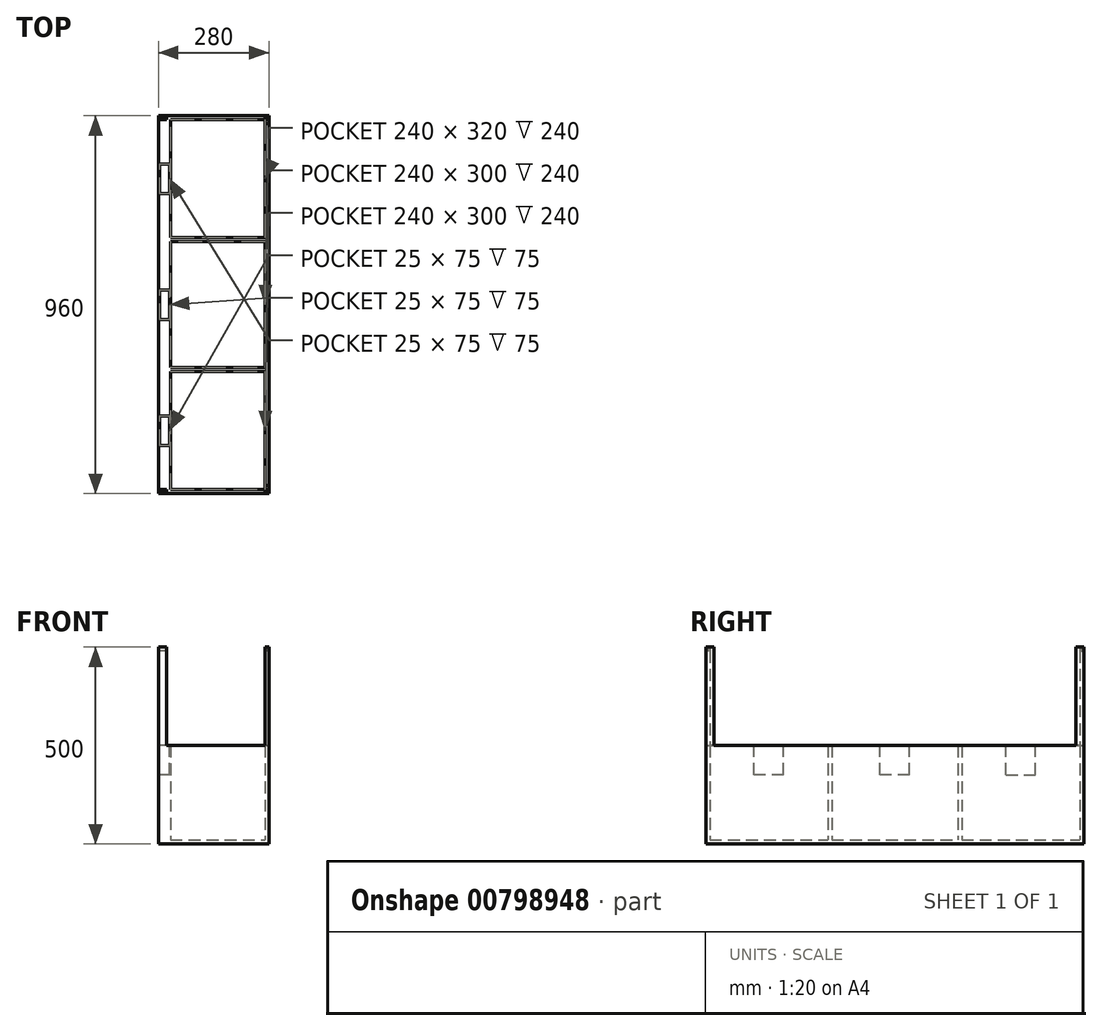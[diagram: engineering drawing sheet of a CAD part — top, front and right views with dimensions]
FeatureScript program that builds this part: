
annotation { "Feature Type Name" : "Feature", "Feature Type Description" : "" }
export const myFeature = defineFeature(function(context is Context, id is Id, definition is map)
    precondition{}
    {
        {
            var Q0;
            Q0=qCreatedBy(makeId("Top.planeOp"),FACE);
            var sketch = newSketch(context, id + "F0", { "sketchPlane" : qUnion([Q0])});
            skLineSegment(sketch, "E0.bottom", {"start": v(130, -480) * mm, "end": v(-130, -480) * mm});
            skLineSegment(sketch, "E0.top", {"start": v(130, 480) * mm, "end": v(-130, 480) * mm});
            skLineSegment(sketch, "E0.left", {"start": v(130, -480) * mm, "end": v(130, 480) * mm});
            skLineSegment(sketch, "E0.right", {"start": v(-130, -480) * mm, "end": v(-130, 480) * mm});
            skPoint(sketch, "E0.middle", {"position": v(0, 0) * mm});
            skLineSegment(sketch, "E1.bottom", {"start": v(-130, 480) * mm, "end": v(-150, 480) * mm});
            skLineSegment(sketch, "E1.top", {"start": v(-130, -480) * mm, "end": v(-150, -480) * mm});
            skLineSegment(sketch, "E1.left", {"start": v(-130, 480) * mm, "end": v(-130, -480) * mm});
            skLineSegment(sketch, "E1.right", {"start": v(-150, 480) * mm, "end": v(-150, -480) * mm});
            skSolve(sketch);
        }
        {
            var Q0;
            Q0=makeQuery(id+"F0.imprint","IMPRINT",FACE,{"disambiguationData":[TD([[makeQuery(id+"F0.imprint","IMPRINT",EDGE,{"derivedFrom":sQuery(id+"F0.wireOp",EDGE,"E0.bottom")}),-1.0]])]});
            extrude(context, id + "F1", {"entities" : qUnion([Q0]), "depth" : 250 * mm, "offsetDistance" : 25 * mm});
        }
        {
            var Q0;
            Q0=makeQuery(id+"F1.opExtrude","CAP_FACE",FACE,{"disambiguationData":[OSD([sQuery(id+"F0.wireOp",EDGE,"E0.bottom"),sQuery(id+"F0.wireOp",EDGE,"E0.top"),sQuery(id+"F0.wireOp",EDGE,"E0.left"),sQuery(id+"F0.wireOp",EDGE,"E0.right")])],"isStart":false});
            shell(context, id + "F2", {"entities" : qUnion([Q0]), "thickness" : 10 * mm});
        }
        {
            var Q0;
            Q0=makeQuery(id+"F2.opShell","OFFSET_FACE",FACE,{"disambiguationData":[OSD([sQuery(id+"F0.wireOp",EDGE,"E0.bottom"),sQuery(id+"F0.wireOp",EDGE,"E0.top"),sQuery(id+"F0.wireOp",EDGE,"E0.left"),sQuery(id+"F0.wireOp",EDGE,"E0.right")])]});
            var sketch = newSketch(context, id + "F3", { "sketchPlane" : qUnion([Q0])});
            skLineSegment(sketch, "E2.bottom", {"start": v(-120, 170) * mm, "end": v(120, 170) * mm});
            skLineSegment(sketch, "E2.top", {"start": v(-120, 160) * mm, "end": v(120, 160) * mm});
            skLineSegment(sketch, "E2.left", {"start": v(-120, 170) * mm, "end": v(-120, 160) * mm});
            skLineSegment(sketch, "E2.right", {"start": v(120, 170) * mm, "end": v(120, 160) * mm});
            skLineSegment(sketch, "E3.bottom", {"start": v(-120, -160) * mm, "end": v(120, -160) * mm});
            skLineSegment(sketch, "E3.top", {"start": v(-120, -170) * mm, "end": v(120, -170) * mm});
            skLineSegment(sketch, "E3.left", {"start": v(-120, -160) * mm, "end": v(-120, -170) * mm});
            skLineSegment(sketch, "E3.right", {"start": v(120, -160) * mm, "end": v(120, -170) * mm});
            skSolve(sketch);
        }
        {
            var Q0;
            Q0=makeQuery(id+"F3.imprint","IMPRINT",FACE,{"disambiguationData":[TD([[makeQuery(id+"F3.imprint","IMPRINT",EDGE,{"derivedFrom":sQuery(id+"F3.wireOp",EDGE,"E3.bottom")}),-1.0]])]});
            var Q1;
            Q1=makeQuery(id+"F3.imprint","IMPRINT",FACE,{"disambiguationData":[TD([[makeQuery(id+"F3.imprint","IMPRINT",EDGE,{"derivedFrom":sQuery(id+"F3.wireOp",EDGE,"E2.bottom")}),-1.0]])]});
            extrude(context, id + "F4", {"entities" : qUnion([Q0, Q1]), "operationType" : NewBodyOperationType.ADD, "depth" : 240 * mm, "offsetDistance" : 25 * mm});
        }
        {
            var Q0;
            Q0=makeQuery(id+"F4.boolean.opBoolean","MERGE",FACE,{"derivedFrom":[makeQuery(id+"F1.opExtrude","CAP_FACE",FACE,{"disambiguationData":[OSD([sQuery(id+"F0.wireOp",EDGE,"E0.bottom"),sQuery(id+"F0.wireOp",EDGE,"E0.top"),sQuery(id+"F0.wireOp",EDGE,"E0.left"),sQuery(id+"F0.wireOp",EDGE,"E0.right")])],"isStart":false}),makeQuery(id+"F4.opExtrude","CAP_FACE",FACE,{"disambiguationData":[OSD([sQuery(id+"F3.wireOp",EDGE,"E2.bottom"),sQuery(id+"F3.wireOp",EDGE,"E2.top"),sQuery(id+"F3.wireOp",EDGE,"E2.left"),sQuery(id+"F3.wireOp",EDGE,"E2.right")])],"isStart":false}),makeQuery(id+"F4.opExtrude","CAP_FACE",FACE,{"disambiguationData":[OSD([sQuery(id+"F3.wireOp",EDGE,"E3.bottom"),sQuery(id+"F3.wireOp",EDGE,"E3.top"),sQuery(id+"F3.wireOp",EDGE,"E3.left"),sQuery(id+"F3.wireOp",EDGE,"E3.right")])],"isStart":false})]});
            var sketch = newSketch(context, id + "F5", { "sketchPlane" : qUnion([Q0])});
            skLineSegment(sketch, "E4.bottom", {"start": v(130, -480) * mm, "end": v(120, -480) * mm});
            skLineSegment(sketch, "E4.top", {"start": v(130, 480) * mm, "end": v(120, 480) * mm});
            skLineSegment(sketch, "E4.left", {"start": v(130, -480) * mm, "end": v(130, 480) * mm});
            skLineSegment(sketch, "E4.right", {"start": v(120, -480) * mm, "end": v(120, 480) * mm});
            skLineSegment(sketch, "E5.top", {"start": v(130, -470) * mm, "end": v(120, -470) * mm});
            skLineSegment(sketch, "E5.left", {"start": v(120, -480) * mm, "end": v(120, -470) * mm});
            skLineSegment(sketch, "E5.right", {"start": v(130, -480) * mm, "end": v(130, -470) * mm});
            skLineSegment(sketch, "E6.top", {"start": v(130, 470) * mm, "end": v(120, 470) * mm});
            skLineSegment(sketch, "E6.left", {"start": v(120, 480) * mm, "end": v(120, 470) * mm});
            skLineSegment(sketch, "E6.right", {"start": v(130, 480) * mm, "end": v(130, 470) * mm});
            skLineSegment(sketch, "E7.bottom", {"start": v(-120, 470) * mm, "end": v(130, 470) * mm});
            skLineSegment(sketch, "E7.top", {"start": v(-120, 460) * mm, "end": v(130, 460) * mm});
            skLineSegment(sketch, "E7.left", {"start": v(130, 470) * mm, "end": v(130, 460) * mm});
            skLineSegment(sketch, "E7.right", {"start": v(-120, 470) * mm, "end": v(-120, 460) * mm});
            skLineSegment(sketch, "E8.bottom", {"start": v(-120, -470) * mm, "end": v(130, -470) * mm});
            skLineSegment(sketch, "E8.top", {"start": v(-120, -460) * mm, "end": v(130, -460) * mm});
            skLineSegment(sketch, "E8.left", {"start": v(130, -470) * mm, "end": v(130, -460) * mm});
            skLineSegment(sketch, "E8.right", {"start": v(-120, -470) * mm, "end": v(-120, -460) * mm});
            skLineSegment(sketch, "E9.bottom", {"start": v(130, -480) * mm, "end": v(-150, -480) * mm});
            skLineSegment(sketch, "E9.top", {"start": v(130, -470) * mm, "end": v(-150, -470) * mm});
            skLineSegment(sketch, "E9.right", {"start": v(-150, -480) * mm, "end": v(-150, -470) * mm});
            skLineSegment(sketch, "E10.bottom", {"start": v(130, 480) * mm, "end": v(-150, 480) * mm});
            skLineSegment(sketch, "E10.top", {"start": v(130, 470) * mm, "end": v(-150, 470) * mm});
            skLineSegment(sketch, "E10.right", {"start": v(-150, 480) * mm, "end": v(-150, 470) * mm});
            skLineSegment(sketch, "E11.bottom", {"start": v(-150, -470) * mm, "end": v(-140, -470) * mm});
            skLineSegment(sketch, "E11.top", {"start": v(-150, -450) * mm, "end": v(-140, -450) * mm});
            skLineSegment(sketch, "E11.left", {"start": v(-150, -470) * mm, "end": v(-150, -450) * mm});
            skLineSegment(sketch, "E11.right", {"start": v(-140, -470) * mm, "end": v(-140, -450) * mm});
            skLineSegment(sketch, "E12.bottom", {"start": v(-150, 470) * mm, "end": v(-140, 470) * mm});
            skLineSegment(sketch, "E12.top", {"start": v(-150, 450) * mm, "end": v(-140, 450) * mm});
            skLineSegment(sketch, "E12.left", {"start": v(-150, 470) * mm, "end": v(-150, 450) * mm});
            skLineSegment(sketch, "E12.right", {"start": v(-140, 470) * mm, "end": v(-140, 450) * mm});
            skSolve(sketch);
        }
        {
            var Q0;
            Q0=makeQuery(id+"F5.imprint","IMPRINT",FACE,{"disambiguationData":[TD([[makeQuery(id+"F5.imprint","IMPRINT",EDGE,{"derivedFrom":sQuery(id+"F5.wireOp",EDGE,"E11.bottom")}),1.0]])]});
            var Q1;
            {var subQ1=sQuery(id+"F5.wireOp",EDGE,"E9.right");Q1=makeQuery(id+"F5.imprint","IMPRINT",FACE,{"disambiguationData":[TD([[makeQuery(id+"F5.imprint","IMPRINT",EDGE,{"derivedFrom":subQ1}),-1.0]])]});}
            var Q2;
            {var subQ1=sQuery(id+"F5.wireOp",EDGE,"E5.left");Q2=makeQuery(id+"F5.imprint","IMPRINT",FACE,{"disambiguationData":[TD([[makeQuery(id+"F5.imprint","IMPRINT",EDGE,{"derivedFrom":subQ1}),1.0]])]});}
            var Q3;
            {var subQ0=sQuery(id+"F5.wireOp",EDGE,"E5.left");Q3=makeQuery(id+"F5.imprint","IMPRINT",FACE,{"disambiguationData":[TD([[makeQuery(id+"F5.imprint","IMPRINT",EDGE,{"derivedFrom":subQ0}),-1.0]])]});}
            var Q4;
            {var subQ5=sQuery(id+"F5.wireOp",EDGE,"E8.left");Q4=makeQuery(id+"F5.imprint","IMPRINT",FACE,{"disambiguationData":[TD([[makeQuery(id+"F5.imprint","IMPRINT",EDGE,{"derivedFrom":subQ5}),1.0]])]});}
            var Q5;
            {var subQ4=sQuery(id+"F5.wireOp",EDGE,"E4.left");Q5=makeQuery(id+"F5.imprint","IMPRINT",FACE,{"disambiguationData":[TD([[makeQuery(id+"F5.imprint","IMPRINT",EDGE,{"derivedFrom":subQ4}),1.0]])]});}
            var Q6;
            {var subQ5=sQuery(id+"F5.wireOp",EDGE,"E7.left");Q6=makeQuery(id+"F5.imprint","IMPRINT",FACE,{"disambiguationData":[TD([[makeQuery(id+"F5.imprint","IMPRINT",EDGE,{"derivedFrom":subQ5}),1.0]])]});}
            var Q7;
            {var subQ0=sQuery(id+"F5.wireOp",EDGE,"E6.left");Q7=makeQuery(id+"F5.imprint","IMPRINT",FACE,{"disambiguationData":[TD([[makeQuery(id+"F5.imprint","IMPRINT",EDGE,{"derivedFrom":subQ0}),1.0]])]});}
            var Q8;
            {var subQ4=sQuery(id+"F5.wireOp",EDGE,"E6.left");Q8=makeQuery(id+"F5.imprint","IMPRINT",FACE,{"disambiguationData":[TD([[makeQuery(id+"F5.imprint","IMPRINT",EDGE,{"derivedFrom":subQ4}),-1.0]])]});}
            var Q9;
            {var subQ4=sQuery(id+"F5.wireOp",EDGE,"E10.right");Q9=makeQuery(id+"F5.imprint","IMPRINT",FACE,{"disambiguationData":[TD([[makeQuery(id+"F5.imprint","IMPRINT",EDGE,{"derivedFrom":subQ4}),1.0]])]});}
            var Q10;
            Q10=makeQuery(id+"F5.imprint","IMPRINT",FACE,{"disambiguationData":[TD([[makeQuery(id+"F5.imprint","IMPRINT",EDGE,{"derivedFrom":sQuery(id+"F5.wireOp",EDGE,"E12.bottom")}),-1.0]])]});
            extrude(context, id + "F6", {"entities" : qUnion([Q0, Q1, Q2, Q3, Q4, Q5, Q6, Q7, Q8, Q9, Q10]), "operationType" : NewBodyOperationType.ADD, "depth" : 250 * mm, "offsetDistance" : 25 * mm});
        }
        {
            var Q0;
            Q0=makeQuery(id+"F0.imprint","IMPRINT",FACE,{"disambiguationData":[TD([[makeQuery(id+"F0.imprint","IMPRINT",EDGE,{"derivedFrom":sQuery(id+"F0.wireOp",EDGE,"E1.bottom")}),1.0]])]});
            extrude(context, id + "F7", {"entities" : qUnion([Q0]), "operationType" : NewBodyOperationType.ADD, "depth" : 250 * mm, "offsetDistance" : 25 * mm});
        }
        {
            var Q0;
            {var subQ0=sQuery(id+"F0.wireOp",EDGE,"E1.left");Q0=makeQuery(id+"F7.boolean.opBoolean","MERGE",FACE,{"derivedFrom":[makeQuery(id+"F4.boolean.opBoolean","MERGE",FACE,{"derivedFrom":[makeQuery(id+"F1.opExtrude","CAP_FACE",FACE,{"disambiguationData":[OSD([sQuery(id+"F0.wireOp",EDGE,"E0.bottom"),sQuery(id+"F0.wireOp",EDGE,"E0.top"),sQuery(id+"F0.wireOp",EDGE,"E0.left"),subQ0])],"isStart":false}),makeQuery(id+"F4.opExtrude","CAP_FACE",FACE,{"disambiguationData":[OSD([sQuery(id+"F3.wireOp",EDGE,"E2.bottom"),sQuery(id+"F3.wireOp",EDGE,"E2.top"),sQuery(id+"F3.wireOp",EDGE,"E2.left"),sQuery(id+"F3.wireOp",EDGE,"E2.right")])],"isStart":false}),makeQuery(id+"F4.opExtrude","CAP_FACE",FACE,{"disambiguationData":[OSD([sQuery(id+"F3.wireOp",EDGE,"E3.bottom"),sQuery(id+"F3.wireOp",EDGE,"E3.top"),sQuery(id+"F3.wireOp",EDGE,"E3.left"),sQuery(id+"F3.wireOp",EDGE,"E3.right")])],"isStart":false})]}),makeQuery(id+"F7.opExtrude","CAP_FACE",FACE,{"disambiguationData":[OSD([sQuery(id+"F0.wireOp",EDGE,"E1.bottom"),sQuery(id+"F0.wireOp",EDGE,"E1.top"),subQ0,sQuery(id+"F0.wireOp",EDGE,"E1.right")])],"isStart":false})]});}
            var sketch = newSketch(context, id + "F8", { "sketchPlane" : qUnion([Q0])});
            skLineSegment(sketch, "E13", {"start": v(-120, 0) * mm, "end": v(0, 0) * mm, "construction": true});
            skLineSegment(sketch, "E14", {"start": v(-120, 320) * mm, "end": v(0, 320) * mm, "construction": true});
            skLineSegment(sketch, "E15", {"start": v(-120, -320) * mm, "end": v(0, -320) * mm, "construction": true});
            skLineSegment(sketch, "E16", {"start": v(-120, 320) * mm, "end": v(-150, 320) * mm, "construction": true});
            skLineSegment(sketch, "E17", {"start": v(-120, 0) * mm, "end": v(-150, 0) * mm, "construction": true});
            skLineSegment(sketch, "E18", {"start": v(-120, -320) * mm, "end": v(-150, -320) * mm, "construction": true});
            skLineSegment(sketch, "E19", {"start": v(-135, 320) * mm, "end": v(-135, -320) * mm, "construction": true});
            skLineSegment(sketch, "E20.bottom", {"start": v(-122.5, 282.5) * mm, "end": v(-147.5, 282.5) * mm});
            skLineSegment(sketch, "E20.top", {"start": v(-122.5, 357.5) * mm, "end": v(-147.5, 357.5) * mm});
            skLineSegment(sketch, "E20.left", {"start": v(-122.5, 282.5) * mm, "end": v(-122.5, 357.5) * mm});
            skLineSegment(sketch, "E20.right", {"start": v(-147.5, 282.5) * mm, "end": v(-147.5, 357.5) * mm});
            skPoint(sketch, "E20.middle", {"position": v(-135, 320) * mm});
            skLineSegment(sketch, "E21.bottom", {"start": v(-122.5, 37.5) * mm, "end": v(-147.5, 37.5) * mm});
            skLineSegment(sketch, "E21.top", {"start": v(-122.5, -37.5) * mm, "end": v(-147.5, -37.5) * mm});
            skLineSegment(sketch, "E21.left", {"start": v(-122.5, 37.5) * mm, "end": v(-122.5, -37.5) * mm});
            skLineSegment(sketch, "E21.right", {"start": v(-147.5, 37.5) * mm, "end": v(-147.5, -37.5) * mm});
            skPoint(sketch, "E21.middle", {"position": v(-135, 0) * mm});
            skLineSegment(sketch, "E22.bottom", {"start": v(-122.5, -282.5) * mm, "end": v(-147.5, -282.5) * mm});
            skLineSegment(sketch, "E22.top", {"start": v(-122.5, -357.5) * mm, "end": v(-147.5, -357.5) * mm});
            skLineSegment(sketch, "E22.left", {"start": v(-122.5, -282.5) * mm, "end": v(-122.5, -357.5) * mm});
            skLineSegment(sketch, "E22.right", {"start": v(-147.5, -282.5) * mm, "end": v(-147.5, -357.5) * mm});
            skPoint(sketch, "E22.middle", {"position": v(-135, -320) * mm});
            skSolve(sketch);
        }
        {
            var Q0;
            Q0=makeQuery(id+"F8.imprint","IMPRINT",FACE,{"disambiguationData":[TD([[makeQuery(id+"F8.imprint","IMPRINT",EDGE,{"derivedFrom":sQuery(id+"F8.wireOp",EDGE,"E20.bottom")}),-1.0]])]});
            var Q1;
            Q1=makeQuery(id+"F8.imprint","IMPRINT",FACE,{"disambiguationData":[TD([[makeQuery(id+"F8.imprint","IMPRINT",EDGE,{"derivedFrom":sQuery(id+"F8.wireOp",EDGE,"E21.bottom")}),1.0]])]});
            var Q2;
            Q2=makeQuery(id+"F8.imprint","IMPRINT",FACE,{"disambiguationData":[TD([[makeQuery(id+"F8.imprint","IMPRINT",EDGE,{"derivedFrom":sQuery(id+"F8.wireOp",EDGE,"E22.bottom")}),1.0]])]});
            extrude(context, id + "F9", {"entities" : qUnion([Q0, Q1, Q2]), "operationType" : NewBodyOperationType.REMOVE, "oppositeDirection" : true, "depth" : 75 * mm, "offsetDistance" : 25 * mm});
        }
        {
            var Q0;
            Q0=makeQuery(id+"F7.boolean.opBoolean","MERGE",FACE,{"derivedFrom":[makeQuery(id+"F6.opExtrude","SWEPT_FACE",FACE,{"disambiguationData":[OSD([sQuery(id+"F5.wireOp",EDGE,"E9.right"),sQuery(id+"F5.wireOp",EDGE,"E11.left")])]}),makeQuery(id+"F6.opExtrude","SWEPT_FACE",FACE,{"disambiguationData":[OSD([sQuery(id+"F5.wireOp",EDGE,"E10.right"),sQuery(id+"F5.wireOp",EDGE,"E12.left")])]}),makeQuery(id+"F7.opExtrude","SWEPT_FACE",FACE,{"disambiguationData":[OSD([sQuery(id+"F0.wireOp",EDGE,"E1.right")])]})]});
            var sketch = newSketch(context, id + "F10", { "sketchPlane" : qUnion([Q0])});
            skLineSegment(sketch, "E23.bottom", {"start": v(-450, 500) * mm, "end": v(-475, 500) * mm});
            skLineSegment(sketch, "E23.top", {"start": v(-450, 490) * mm, "end": v(-475, 490) * mm});
            skLineSegment(sketch, "E23.left", {"start": v(-450, 500) * mm, "end": v(-450, 490) * mm});
            skLineSegment(sketch, "E23.right", {"start": v(-475, 500) * mm, "end": v(-475, 490) * mm});
            skLineSegment(sketch, "E24.bottom", {"start": v(450, 500) * mm, "end": v(475, 500) * mm});
            skLineSegment(sketch, "E24.top", {"start": v(450, 490) * mm, "end": v(475, 490) * mm});
            skLineSegment(sketch, "E24.left", {"start": v(450, 500) * mm, "end": v(450, 490) * mm});
            skLineSegment(sketch, "E24.right", {"start": v(475, 500) * mm, "end": v(475, 490) * mm});
            skLineSegment(sketch, "E25.bottom", {"start": v(-450, 500) * mm, "end": v(450, 500) * mm});
            skLineSegment(sketch, "E25.top", {"start": v(-450, 490) * mm, "end": v(450, 490) * mm});
            skSolve(sketch);
        }
        {
            var Q0;
            Q0=makeQuery(id+"F10.imprint","IMPRINT",FACE,{"disambiguationData":[TD([[makeQuery(id+"F10.imprint","IMPRINT",EDGE,{"derivedFrom":sQuery(id+"F10.wireOp",EDGE,"E24.bottom")}),1.0]])]});
            var Q1;
            Q1=makeQuery(id+"F10.imprint","IMPRINT",FACE,{"disambiguationData":[TD([[makeQuery(id+"F10.imprint","IMPRINT",EDGE,{"derivedFrom":sQuery(id+"F10.wireOp",EDGE,"E23.bottom")}),-1.0]])]});
            var Q2;
            Q2=makeQuery(id+"F10.imprint","IMPRINT",FACE,{"disambiguationData":[TD([[makeQuery(id+"F10.imprint","IMPRINT",EDGE,{"derivedFrom":sQuery(id+"F10.wireOp",EDGE,"E25.bottom")}),-1.0]])]});
            extrude(context, id + "F11", {"entities" : qUnion([Q0, Q1, Q2]), "operationType" : NewBodyOperationType.REMOVE, "oppositeDirection" : true, "depth" : 275 * mm, "offsetDistance" : 25 * mm});
        }
    });
